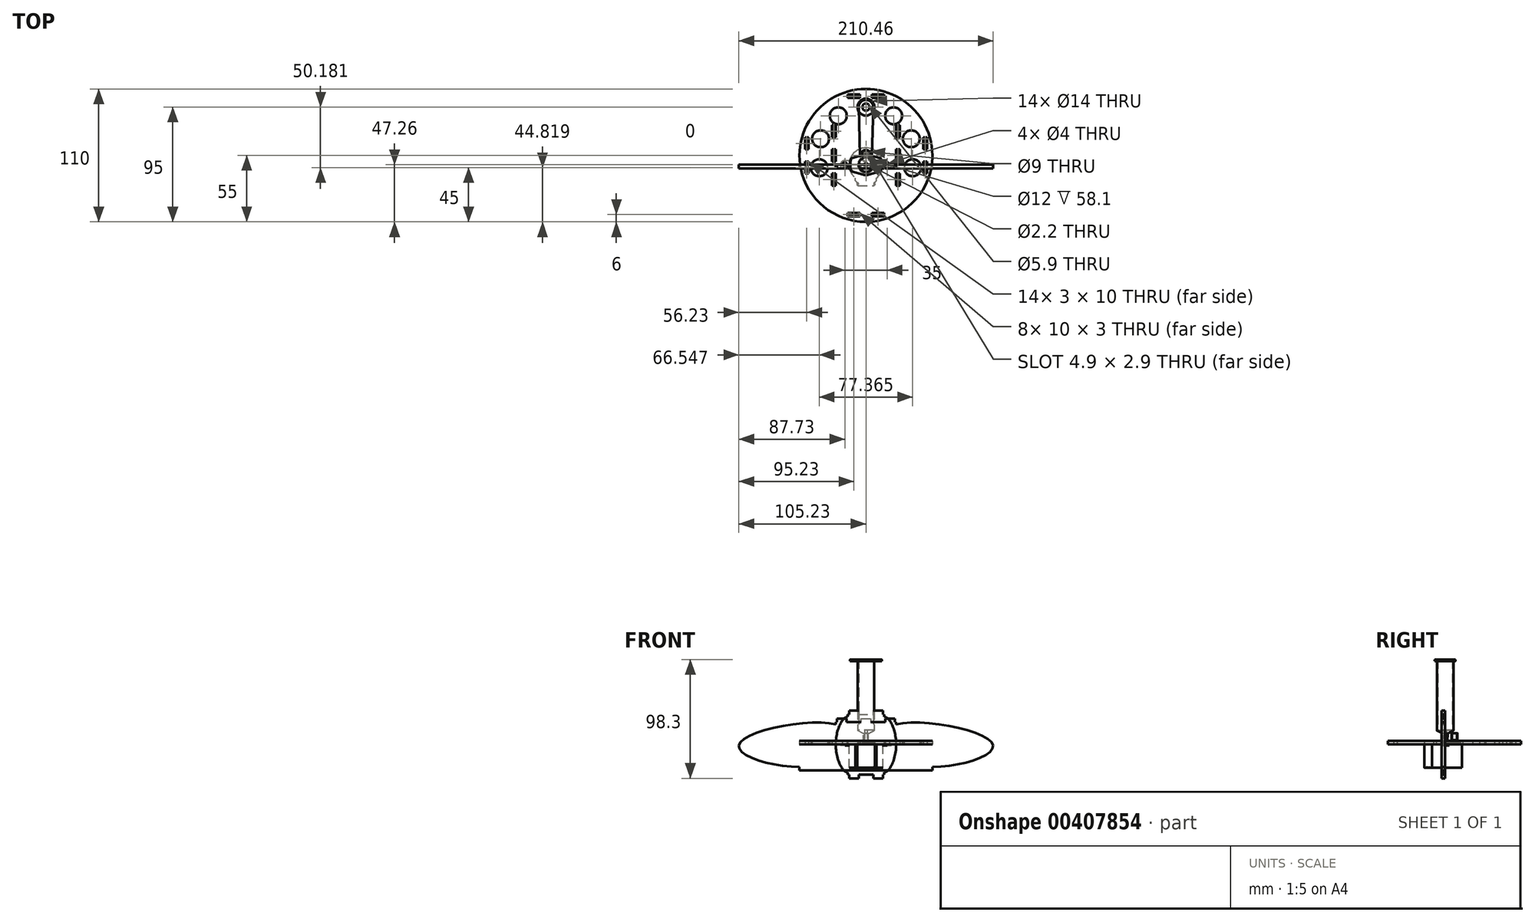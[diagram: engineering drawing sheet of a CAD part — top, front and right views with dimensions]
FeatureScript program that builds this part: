
annotation { "Feature Type Name" : "Feature", "Feature Type Description" : "" }
export const myFeature = defineFeature(function(context is Context, id is Id, definition is map)
    precondition{}
    {
        {
            var Q0;
            Q0=qCreatedBy(makeId("Top.planeOp"),FACE);
            var sketch = newSketch(context, id + "F0", { "sketchPlane" : qUnion([Q0])});
            skCircle(sketch, "E0", {"center": v(0, 0) * mm, "radius": 6.85 * mm});
            skCircle(sketch, "E1", {"center": v(0, 0) * mm, "radius": 1.1 * mm});
            skCircle(sketch, "E2", {"center": v(0, 0) * mm, "radius": 8.5 * mm});
            skLineSegment(sketch, "E3", {"start": v(-1.1, 0) * mm, "end": v(1.1, 0) * mm});
            skLineSegment(sketch, "E4", {"start": v(-11.5, 5.5) * mm, "end": v(-11.4, 5.5) * mm});
            skLineSegment(sketch, "E5", {"start": v(11.5, -5.5) * mm, "end": v(11.4, -5.5) * mm});
            skLineSegment(sketch, "E6", {"start": v(-11.5, 5.5) * mm, "end": v(-2.38, 8.16) * mm});
            skLineSegment(sketch, "E7", {"start": v(-11.5, -5.5) * mm, "end": v(-2.38, -8.16) * mm});
            skLineSegment(sketch, "E8", {"start": v(11.5, -5.5) * mm, "end": v(2.38, -8.16) * mm});
            skLineSegment(sketch, "E9", {"start": v(11.5, 5.5) * mm, "end": v(2.38, 8.16) * mm});
            skFitSpline(sketch, "E10", {"points": [v(-11.5, 5.5) * mm, v(-13.25, 0) * mm, v(-11.5, -5.5) * mm, v(-8.5, 0) * mm, v(-11.5, 5.5) * mm]});
            skFitSpline(sketch, "E11", {"points": [v(11.5, 5.5) * mm, v(13.25, 0) * mm, v(11.5, -5.5) * mm, v(8.5, 0) * mm, v(11.5, 5.5) * mm]});
            skLineSegment(sketch, "E12.trimOffspring", {"start": v(-11.4, -5.5) * mm, "end": v(-11.5, -5.5) * mm});
            skLineSegment(sketch, "E13.trimOffspring", {"start": v(11.4, 5.5) * mm, "end": v(11.5, 5.5) * mm});
            skCircle(sketch, "E14", {"center": v(0, 0) * mm, "radius": 6 * mm});
            skCircle(sketch, "E15", {"center": v(0, 0) * mm, "radius": 2 * mm});
            skSolve(sketch);
        }
        {
            var Q0;
            Q0=qSketchRegion(id+"F0",true);
            extrude(context, id + "F1", {"entities" : qUnion([Q0]), "depth" : 70.3 * mm});
        }
        {
            var Q0;
            Q0=qSketchRegion(id+"F0",true);
            extrude(context, id + "F2", {"entities" : qUnion([Q0]), "operationType" : NewBodyOperationType.REMOVE, "depth" : (70.3 - 1.4) * mm});
        }
        {
            var Q0;
            Q0=makeQuery(id+"F0.imprint","IMPRINT",FACE,{"disambiguationData":[TD([[makeQuery(id+"F0.imprint","IMPRINT",EDGE,{"derivedFrom":sQuery(id+"F0.wireOp",EDGE,"E0")}),1.0]])]});
            extrude(context, id + "F3", {"entities" : qUnion([Q0]), "operationType" : NewBodyOperationType.ADD, "depth" : 70.3 * mm, "hasSecondDirection" : true, "secondDirectionOppositeDirection" : true, "secondDirectionDepth" : -9 * mm});
        }
        {
            var Q0;
            Q0=makeQuery(id+"F0.imprint","IMPRINT",FACE,{"disambiguationData":[TD([[makeQuery(id+"F0.imprint","IMPRINT",EDGE,{"derivedFrom":sQuery(id+"F0.wireOp",EDGE,"E14")}),1.0]])]});
            extrude(context, id + "F4", {"entities" : qUnion([Q0]), "operationType" : NewBodyOperationType.ADD, "depth" : 12 * mm, "hasSecondDirection" : true, "secondDirectionOppositeDirection" : true, "secondDirectionDepth" : -9 * mm});
        }
        {
            var Q0;
            Q0=makeQuery(id+"F0.imprint","IMPRINT",FACE,{"disambiguationData":[TD([[makeQuery(id+"F0.imprint","IMPRINT",EDGE,{"derivedFrom":sQuery(id+"F0.wireOp",EDGE,"E15")}),1.0]])]});
            extrude(context, id + "F5", {"entities" : qUnion([Q0]), "operationType" : NewBodyOperationType.ADD, "depth" : 12 * mm});
        }
        {
            var Q0;
            Q0=makeQuery(id+"F3.opExtrude","CAP_EDGE",EDGE,{"disambiguationData":[OSD([sQuery(id+"F0.wireOp",EDGE,"E0")])],"isStart":true});
            chamfer(context, id + "F6", {"entities" : qUnion([Q0]), "chamferType" : ChamferType.TWO_OFFSETS, "width1" : 2.5 * mm, "oppositeDirection" : false, "width2" : 4.9 * mm, "tangentPropagation" : true});
        }
        {
            var Q0;
            Q0=makeQuery(id+"F5.opExtrude","CAP_EDGE",EDGE,{"disambiguationData":[OSD([sQuery(id+"F0.wireOp",EDGE,"E15")])],"isStart":true});
            chamfer(context, id + "F7", {"entities" : qUnion([Q0]), "chamferType" : ChamferType.TWO_OFFSETS, "width1" : 9 * mm, "oppositeDirection" : false, "width2" : 0.1 * mm, "tangentPropagation" : true});
        }
        {
            var Q0;
            Q0=makeQuery(id+"F5.opExtrude","CAP_EDGE",EDGE,{"disambiguationData":[OSD([sQuery(id+"F0.wireOp",EDGE,"E1")])],"isStart":true});
            var Q1;
            {var subQ0=sQuery(id+"F0.wireOp",EDGE,"E15");Q1=makeQuery(id+"F7.opChamfer","BLEND_EDGE",EDGE,{"blendedFrom":[makeQuery(id+"F5.opExtrude","CAP_EDGE",EDGE,{"disambiguationData":[OSD([subQ0])],"isStart":true}),makeQuery(id+"F5.opExtrude","CAP_FACE",FACE,{"disambiguationData":[OSD([sQuery(id+"F0.wireOp",EDGE,"E1"),subQ0])],"isStart":true})],"blendedInto":[makeQuery(id+"F5.opExtrude","CAP_FACE",FACE,{"disambiguationData":[OSD([sQuery(id+"F0.wireOp",EDGE,"E1"),subQ0])],"isStart":true})]});}
            var Q2;
            {var subQ0=sQuery(id+"F0.wireOp",EDGE,"E0");Q2=makeQuery(id+"F6.opChamfer","BLEND_EDGE",EDGE,{"blendedFrom":[makeQuery(id+"F3.opExtrude","CAP_EDGE",EDGE,{"disambiguationData":[OSD([subQ0])],"isStart":true}),makeQuery(id+"F3.opExtrude","SWEPT_FACE",FACE,{"disambiguationData":[OSD([subQ0])]})],"blendedInto":[makeQuery(id+"F3.opExtrude","SWEPT_FACE",FACE,{"disambiguationData":[OSD([subQ0])]})]});}
            var Q3;
            {var subQ0=sQuery(id+"F0.wireOp",EDGE,"E15");Q3=makeQuery(id+"F7.opChamfer","BLEND_EDGE",EDGE,{"blendedFrom":[makeQuery(id+"F5.opExtrude","CAP_EDGE",EDGE,{"disambiguationData":[OSD([subQ0])],"isStart":true}),makeQuery(id+"F5.opExtrude","SWEPT_FACE",FACE,{"disambiguationData":[OSD([subQ0])]})],"blendedInto":[makeQuery(id+"F5.opExtrude","SWEPT_FACE",FACE,{"disambiguationData":[OSD([subQ0])]})]});}
            var Q4;
            Q4=makeQuery(id+"F3.opExtrude","CAP_EDGE",EDGE,{"disambiguationData":[OSD([sQuery(id+"F0.wireOp",EDGE,"E14")])],"isStart":false});
            var Q5;
            Q5=makeQuery(id+"F1.opExtrude","CAP_EDGE",EDGE,{"disambiguationData":[OSD([sQuery(id+"F0.wireOp",EDGE,"E9")])],"isStart":false});
            var Q6;
            Q6=makeQuery(id+"F1.opExtrude","CAP_EDGE",EDGE,{"disambiguationData":[OSD([sQuery(id+"F0.wireOp",EDGE,"E11")])],"isStart":false});
            var Q7;
            Q7=makeQuery(id+"F1.opExtrude","CAP_EDGE",EDGE,{"disambiguationData":[OSD([sQuery(id+"F0.wireOp",EDGE,"E8")])],"isStart":false});
            var Q8;
            {var subQ0=sQuery(id+"F0.wireOp",EDGE,"E2");Q8=makeQuery(id+"F1.opExtrude","CAP_EDGE",EDGE,{"disambiguationData":[OSD([subQ0]),TDD([makeQuery(id+"F0.imprint","IMPRINT",EDGE,{"disambiguationData":[TD([[makeQuery(id+"F0.imprint","INTERSECT",VERTEX,{"derivedFrom":[subQ0,sQuery(id+"F0.wireOp",EDGE,"E7")]}),-1.0]])],"derivedFrom":subQ0})])],"isStart":false});}
            var Q9;
            Q9=makeQuery(id+"F1.opExtrude","CAP_EDGE",EDGE,{"disambiguationData":[OSD([sQuery(id+"F0.wireOp",EDGE,"E7")])],"isStart":false});
            var Q10;
            Q10=makeQuery(id+"F1.opExtrude","CAP_EDGE",EDGE,{"disambiguationData":[OSD([sQuery(id+"F0.wireOp",EDGE,"E10")])],"isStart":false});
            var Q11;
            Q11=makeQuery(id+"F1.opExtrude","CAP_EDGE",EDGE,{"disambiguationData":[OSD([sQuery(id+"F0.wireOp",EDGE,"E6")])],"isStart":false});
            var Q12;
            {var subQ0=sQuery(id+"F0.wireOp",EDGE,"E2");Q12=makeQuery(id+"F1.opExtrude","CAP_EDGE",EDGE,{"disambiguationData":[OSD([subQ0]),TDD([makeQuery(id+"F0.imprint","IMPRINT",EDGE,{"disambiguationData":[TD([[makeQuery(id+"F0.imprint","INTERSECT",VERTEX,{"derivedFrom":[subQ0,sQuery(id+"F0.wireOp",EDGE,"E6")]}),1.0]])],"derivedFrom":subQ0})])],"isStart":false});}
            var Q13;
            Q13=makeQuery(id+"F2.boolean.opBoolean","COPY",EDGE,{"derivedFrom":makeQuery(id+"F2.opExtrude","CAP_EDGE",EDGE,{"disambiguationData":[OSD([sQuery(id+"F0.wireOp",EDGE,"E7")])],"isStart":false})});
            var Q14;
            {var subQ0=sQuery(id+"F0.wireOp",EDGE,"E2");Q14=makeQuery(id+"F2.boolean.opBoolean","COPY",EDGE,{"derivedFrom":makeQuery(id+"F2.opExtrude","CAP_EDGE",EDGE,{"disambiguationData":[OSD([subQ0]),TDD([makeQuery(id+"F0.imprint","IMPRINT",EDGE,{"disambiguationData":[TD([[makeQuery(id+"F0.imprint","INTERSECT",VERTEX,{"derivedFrom":[subQ0,sQuery(id+"F0.wireOp",EDGE,"E7")]}),-1.0]])],"derivedFrom":subQ0})])],"isStart":false})});}
            var Q15;
            Q15=makeQuery(id+"F2.boolean.opBoolean","COPY",EDGE,{"derivedFrom":makeQuery(id+"F2.opExtrude","CAP_EDGE",EDGE,{"disambiguationData":[OSD([sQuery(id+"F0.wireOp",EDGE,"E8")])],"isStart":false})});
            var Q16;
            Q16=makeQuery(id+"F2.boolean.opBoolean","COPY",EDGE,{"derivedFrom":makeQuery(id+"F2.opExtrude","CAP_EDGE",EDGE,{"disambiguationData":[OSD([sQuery(id+"F0.wireOp",EDGE,"E11")])],"isStart":false})});
            var Q17;
            Q17=makeQuery(id+"F2.boolean.opBoolean","COPY",EDGE,{"derivedFrom":makeQuery(id+"F2.opExtrude","CAP_EDGE",EDGE,{"disambiguationData":[OSD([sQuery(id+"F0.wireOp",EDGE,"E9")])],"isStart":false})});
            var Q18;
            Q18=makeQuery(id+"F2.boolean.opBoolean","COPY",EDGE,{"derivedFrom":makeQuery(id+"F2.opExtrude","CAP_EDGE",EDGE,{"disambiguationData":[OSD([sQuery(id+"F0.wireOp",EDGE,"E10")])],"isStart":false})});
            var Q19;
            Q19=makeQuery(id+"F2.boolean.opBoolean","COPY",EDGE,{"derivedFrom":makeQuery(id+"F2.opExtrude","CAP_EDGE",EDGE,{"disambiguationData":[OSD([sQuery(id+"F0.wireOp",EDGE,"E6")])],"isStart":false})});
            var Q20;
            {var subQ0=sQuery(id+"F0.wireOp",EDGE,"E2");Q20=makeQuery(id+"F2.boolean.opBoolean","COPY",EDGE,{"derivedFrom":makeQuery(id+"F2.opExtrude","CAP_EDGE",EDGE,{"disambiguationData":[OSD([subQ0]),TDD([makeQuery(id+"F0.imprint","IMPRINT",EDGE,{"disambiguationData":[TD([[makeQuery(id+"F0.imprint","INTERSECT",VERTEX,{"derivedFrom":[subQ0,sQuery(id+"F0.wireOp",EDGE,"E6")]}),1.0]])],"derivedFrom":subQ0})])],"isStart":false})});}
            var Q21;
            Q21=makeQuery(id+"F2.boolean.opBoolean","COPY",EDGE,{"derivedFrom":makeQuery(id+"F2.opExtrude","CAP_EDGE",EDGE,{"disambiguationData":[OSD([sQuery(id+"F0.wireOp",EDGE,"E0")])],"isStart":false})});
            fillet(context, id + "F8", {"entities" : qUnion([Q0, Q1, Q2, Q3, Q4, Q5, Q6, Q7, Q8, Q9, Q10, Q11, Q12, Q13, Q14, Q15, Q16, Q17, Q18, Q19, Q20, Q21]), "radius" : 0.2 * mm, "tangentPropagation" : true, "allowEdgeOverflow" : false});
        }
        {
            var Q0;
            Q0=qCreatedBy(makeId("Top.planeOp"),FACE);
            var sketch = newSketch(context, id + "F9", { "sketchPlane" : qUnion([Q0])});
            skCircle(sketch, "E16", {"center": v(0, 0) * mm, "radius": 14 * mm});
            skLineSegment(sketch, "E17", {"start": v(0, 0) * mm, "end": v(0, -13.2) * mm, "construction": true});
            skLineSegment(sketch, "E18", {"start": v(-7.3, -17.2) * mm, "end": v(7.3, -17.2) * mm});
            skLineSegment(sketch, "E19", {"start": v(-7.3, -14.7) * mm, "end": v(7.3, -14.7) * mm, "construction": true});
            skLineSegment(sketch, "E20", {"start": v(7.3, -17.2) * mm, "end": v(7.3, -14.7) * mm});
            skLineSegment(sketch, "E21", {"start": v(-7.3, -17.2) * mm, "end": v(-7.3, -14.7) * mm});
            skLineSegment(sketch, "E22", {"start": v(-8.75, -13.2) * mm, "end": v(-4.66, -13.2) * mm, "construction": true});
            skLineSegment(sketch, "E23", {"start": v(0, -14.7) * mm, "end": v(0, -13.2) * mm});
            skLineSegment(sketch, "E24", {"start": v(7.3, -14.7) * mm, "end": v(8.75, -13.2) * mm});
            skLineSegment(sketch, "E25", {"start": v(8.75, -13.2) * mm, "end": v(8.75, -10.93) * mm});
            skLineSegment(sketch, "E26", {"start": v(-7.3, -14.7) * mm, "end": v(-8.75, -13.2) * mm});
            skLineSegment(sketch, "E27", {"start": v(-8.75, -13.2) * mm, "end": v(-8.75, -10.93) * mm});
            skLineSegment(sketch, "E28", {"start": v(-17.5, 0) * mm, "end": v(17.5, 0) * mm, "construction": true});
            skCircle(sketch, "E29", {"center": v(-17.5, 0) * mm, "radius": 2 * mm});
            skCircle(sketch, "E30", {"center": v(17.5, 0) * mm, "radius": 2 * mm});
            skArc(sketch, "E31", {"start": v(-17.5, 3.5) * mm, "mid": v(-21, 0) * mm, "end": v(-17.5, -3.5) * mm});
            skArc(sketch, "E32", {"start": v(17.5, -3.5) * mm, "mid": v(21, 0) * mm, "end": v(17.5, 3.5) * mm});
            skLineSegment(sketch, "E33", {"start": v(-17.5, 3.5) * mm, "end": v(-13.56, 3.5) * mm});
            skLineSegment(sketch, "E34", {"start": v(-17.5, -3.5) * mm, "end": v(-13.56, -3.5) * mm});
            skLineSegment(sketch, "E35", {"start": v(17.5, -3.5) * mm, "end": v(13.56, -3.5) * mm});
            skLineSegment(sketch, "E36", {"start": v(17.5, 3.5) * mm, "end": v(13.56, 3.5) * mm});
            skCircle(sketch, "E37", {"center": v(0, 7.74) * mm, "radius": 4.5 * mm});
            skCircle(sketch, "E38", {"center": v(0, 7.74) * mm, "radius": 2.45 * mm});
            skLineSegment(sketch, "E39.trimOffspring", {"start": v(4.66, -13.2) * mm, "end": v(8.75, -13.2) * mm, "construction": true});
            skLineSegment(sketch, "E40.trimOffspring", {"start": v(0, -14) * mm, "end": v(0, -17.2) * mm, "construction": true});
            skLineSegment(sketch, "E41", {"start": v(-1.45, 7.74) * mm, "end": v(1.45, 7.74) * mm, "construction": true});
            skLineSegment(sketch, "E42", {"start": v(-1.45, 9.71) * mm, "end": v(-1.45, 5.77) * mm});
            skLineSegment(sketch, "E43", {"start": v(1.45, 9.71) * mm, "end": v(1.45, 5.77) * mm});
            skSolve(sketch);
        }
        {
            var Q0;
            Q0=makeQuery(id+"F9.imprint","IMPRINT",FACE,{"disambiguationData":[TD([[makeQuery(id+"F9.imprint","IMPRINT",EDGE,{"derivedFrom":sQuery(id+"F9.wireOp",EDGE,"E29")}),-1.0]])]});
            var Q1;
            Q1=makeQuery(id+"F9.imprint","IMPRINT",FACE,{"disambiguationData":[TD([[makeQuery(id+"F9.imprint","IMPRINT",EDGE,{"derivedFrom":sQuery(id+"F9.wireOp",EDGE,"E37")}),-1.0]])]});
            var Q2;
            Q2=makeQuery(id+"F9.imprint","IMPRINT",FACE,{"disambiguationData":[TD([[makeQuery(id+"F9.imprint","IMPRINT",EDGE,{"derivedFrom":sQuery(id+"F9.wireOp",EDGE,"E18")}),1.0]])]});
            var Q3;
            Q3=makeQuery(id+"F9.imprint","IMPRINT",FACE,{"disambiguationData":[TD([[makeQuery(id+"F9.imprint","IMPRINT",EDGE,{"derivedFrom":sQuery(id+"F9.wireOp",EDGE,"E30")}),-1.0]])]});
            var Q4;
            Q4=makeQuery(id+"F9.imprint","IMPRINT",FACE,{"disambiguationData":[TD([[makeQuery(id+"F9.imprint","IMPRINT",EDGE,{"derivedFrom":sQuery(id+"F9.wireOp",EDGE,"E37")}),1.0]])]});
            var Q5;
            {var subQ0=sQuery(id+"F9.wireOp",EDGE,"E42");Q5=makeQuery(id+"F9.imprint","IMPRINT",FACE,{"disambiguationData":[TD([[makeQuery(id+"F9.imprint","IMPRINT",EDGE,{"derivedFrom":subQ0}),1.0]])]});}
            var Q6;
            {var subQ0=sQuery(id+"F9.wireOp",EDGE,"E42");Q6=makeQuery(id+"F9.imprint","IMPRINT",FACE,{"disambiguationData":[TD([[makeQuery(id+"F9.imprint","IMPRINT",EDGE,{"derivedFrom":subQ0}),-1.0]])]});}
            var Q7;
            {var subQ0=sQuery(id+"F9.wireOp",EDGE,"E43");Q7=makeQuery(id+"F9.imprint","IMPRINT",FACE,{"disambiguationData":[TD([[makeQuery(id+"F9.imprint","IMPRINT",EDGE,{"derivedFrom":subQ0}),1.0]])]});}
            extrude(context, id + "F10", {"entities" : qUnion([Q0, Q1, Q2, Q3, Q4, Q5, Q6, Q7]), "oppositeDirection" : true, "depth" : 19.3 * mm});
        }
        {
            var Q0;
            Q0=makeQuery(id+"F9.imprint","IMPRINT",FACE,{"disambiguationData":[TD([[makeQuery(id+"F9.imprint","IMPRINT",EDGE,{"derivedFrom":sQuery(id+"F9.wireOp",EDGE,"E29")}),-1.0]])]});
            var Q1;
            Q1=makeQuery(id+"F9.imprint","IMPRINT",FACE,{"disambiguationData":[TD([[makeQuery(id+"F9.imprint","IMPRINT",EDGE,{"derivedFrom":sQuery(id+"F9.wireOp",EDGE,"E30")}),-1.0]])]});
            extrude(context, id + "F11", {"entities" : qUnion([Q0, Q1]), "operationType" : NewBodyOperationType.REMOVE, "endBound" : BoundingType.THROUGH_ALL, "oppositeDirection" : true, "depth" : 25 * mm, "hasSecondDirection" : true, "secondDirectionOppositeDirection" : false, "secondDirectionDepth" : -0.8 * mm});
        }
        {
            var Q0;
            Q0=makeQuery(id+"F9.imprint","IMPRINT",FACE,{"disambiguationData":[TD([[makeQuery(id+"F9.imprint","IMPRINT",EDGE,{"derivedFrom":sQuery(id+"F9.wireOp",EDGE,"E37")}),1.0]])]});
            extrude(context, id + "F12", {"entities" : qUnion([Q0]), "operationType" : NewBodyOperationType.ADD, "depth" : 1.5 * mm});
        }
        {
            var Q0;
            {var subQ0=sQuery(id+"F9.wireOp",EDGE,"E42");Q0=makeQuery(id+"F9.imprint","IMPRINT",FACE,{"disambiguationData":[TD([[makeQuery(id+"F9.imprint","IMPRINT",EDGE,{"derivedFrom":subQ0}),-1.0]])]});}
            var Q1;
            {var subQ0=sQuery(id+"F9.wireOp",EDGE,"E43");Q1=makeQuery(id+"F9.imprint","IMPRINT",FACE,{"disambiguationData":[TD([[makeQuery(id+"F9.imprint","IMPRINT",EDGE,{"derivedFrom":subQ0}),1.0]])]});}
            extrude(context, id + "F13", {"entities" : qUnion([Q0, Q1]), "operationType" : NewBodyOperationType.ADD, "depth" : 3.5 * mm});
        }
        {
            var Q0;
            {var subQ0=sQuery(id+"F9.wireOp",EDGE,"E42");Q0=makeQuery(id+"F9.imprint","IMPRINT",FACE,{"disambiguationData":[TD([[makeQuery(id+"F9.imprint","IMPRINT",EDGE,{"derivedFrom":subQ0}),1.0]])]});}
            extrude(context, id + "F14", {"entities" : qUnion([Q0]), "operationType" : NewBodyOperationType.ADD, "depth" : 9.5 * mm});
        }
        {
            var Q0;
            Q0=makeQuery(id+"F10.opExtrude","CAP_EDGE",EDGE,{"disambiguationData":[OSD([sQuery(id+"F9.wireOp",EDGE,"E18")])],"isStart":false});
            var Q1;
            {var subQ0=sQuery(id+"F9.wireOp",EDGE,"E38");Q1=makeQuery(id+"F14.opExtrude","CAP_EDGE",EDGE,{"disambiguationData":[OSD([subQ0]),TDD([makeQuery(id+"F9.imprint","IMPRINT",EDGE,{"disambiguationData":[TD([[makeQuery(id+"F9.imprint","INTERSECT",VERTEX,{"disambiguationData":[OD(1.0)],"derivedFrom":[subQ0,sQuery(id+"F9.wireOp",EDGE,"E42")]}),-1.0]])],"derivedFrom":subQ0})])],"isStart":false});}
            var Q2;
            {var subQ0=sQuery(id+"F9.wireOp",EDGE,"E42");var subQ1=sQuery(id+"F9.wireOp",EDGE,"E38");Q2=makeQuery(id+"F13.opExtrude","CAP_EDGE",EDGE,{"disambiguationData":[OSD([subQ1]),TDD([makeQuery(id+"F9.imprint","IMPRINT",EDGE,{"disambiguationData":[TD([[makeQuery(id+"F9.imprint","INTERSECT",VERTEX,{"disambiguationData":[OD(0.0)],"derivedFrom":[subQ1,subQ0]}),-1.0]])],"derivedFrom":subQ1})])],"isStart":false});}
            var Q3;
            {var subQ0=sQuery(id+"F9.wireOp",EDGE,"E43");var subQ1=sQuery(id+"F9.wireOp",EDGE,"E38");Q3=makeQuery(id+"F13.opExtrude","CAP_EDGE",EDGE,{"disambiguationData":[OSD([subQ1]),TDD([makeQuery(id+"F9.imprint","IMPRINT",EDGE,{"disambiguationData":[TD([[makeQuery(id+"F9.imprint","INTERSECT",VERTEX,{"disambiguationData":[OD(0.0)],"derivedFrom":[subQ1,subQ0]}),1.0]])],"derivedFrom":subQ1})])],"isStart":false});}
            var Q4;
            {var subQ0=sQuery(id+"F9.wireOp",EDGE,"E38");Q4=makeQuery(id+"F14.opExtrude","CAP_EDGE",EDGE,{"disambiguationData":[OSD([subQ0]),TDD([makeQuery(id+"F9.imprint","IMPRINT",EDGE,{"disambiguationData":[TD([[makeQuery(id+"F9.imprint","INTERSECT",VERTEX,{"disambiguationData":[OD(0.0)],"derivedFrom":[subQ0,sQuery(id+"F9.wireOp",EDGE,"E42")]}),1.0]])],"derivedFrom":subQ0})])],"isStart":false});}
            fillet(context, id + "F15", {"entities" : qUnion([Q0, Q1, Q2, Q3, Q4]), "radius" : 0.3 * mm, "tangentPropagation" : true, "allowEdgeOverflow" : false});
        }
        {
            var Q0;
            Q0=makeQuery(id+"F10.opExtrude","SWEPT_EDGE",EDGE,{"disambiguationData":[OSD([sQuery(id+"F9.wireOp",EDGE,"E18"),sQuery(id+"F9.wireOp",EDGE,"E20")])]});
            var Q1;
            Q1=makeQuery(id+"F10.opExtrude","SWEPT_EDGE",EDGE,{"disambiguationData":[OSD([sQuery(id+"F9.wireOp",EDGE,"E18"),sQuery(id+"F9.wireOp",EDGE,"E21")])]});
            var Q2;
            {var subQ0=sQuery(id+"F9.wireOp",EDGE,"E18");Q2=makeQuery(id+"F15.opFillet","BLEND_EDGE",EDGE,{"blendedFrom":[makeQuery(id+"F10.opExtrude","CAP_EDGE",EDGE,{"disambiguationData":[OSD([subQ0])],"isStart":false}),makeQuery(id+"F10.opExtrude","SWEPT_FACE",FACE,{"disambiguationData":[OSD([subQ0])]})],"blendedInto":[makeQuery(id+"F10.opExtrude","SWEPT_FACE",FACE,{"disambiguationData":[OSD([subQ0])]})]});}
            fillet(context, id + "F16", {"entities" : qUnion([Q0, Q1, Q2]), "radius" : 1 * mm, "tangentPropagation" : true, "allowEdgeOverflow" : false});
        }
        {
            var Q0;
            Q0=makeQuery(id+"F10.opExtrude","SWEPT_EDGE",EDGE,{"disambiguationData":[OSD([sQuery(id+"F9.wireOp",EDGE,"E26"),sQuery(id+"F9.wireOp",EDGE,"E27")])]});
            var Q1;
            Q1=makeQuery(id+"F10.opExtrude","SWEPT_EDGE",EDGE,{"disambiguationData":[OSD([sQuery(id+"F9.wireOp",EDGE,"E21"),sQuery(id+"F9.wireOp",EDGE,"E26")])]});
            var Q2;
            Q2=makeQuery(id+"F10.opExtrude","SWEPT_EDGE",EDGE,{"disambiguationData":[OSD([sQuery(id+"F9.wireOp",EDGE,"E24"),sQuery(id+"F9.wireOp",EDGE,"E25")])]});
            var Q3;
            Q3=makeQuery(id+"F10.opExtrude","SWEPT_EDGE",EDGE,{"disambiguationData":[OSD([sQuery(id+"F9.wireOp",EDGE,"E20"),sQuery(id+"F9.wireOp",EDGE,"E24")])]});
            var Q4;
            Q4=makeQuery(id+"F16.opFillet","BLEND_EDGE",EDGE,{"blendedFrom":[makeQuery(id+"F10.opExtrude","CAP_EDGE",EDGE,{"disambiguationData":[OSD([sQuery(id+"F9.wireOp",EDGE,"E20")])],"isStart":false}),makeQuery(id+"F10.opExtrude","SWEPT_FACE",FACE,{"disambiguationData":[OSD([sQuery(id+"F9.wireOp",EDGE,"E24")])]})],"blendedInto":[makeQuery(id+"F10.opExtrude","SWEPT_FACE",FACE,{"disambiguationData":[OSD([sQuery(id+"F9.wireOp",EDGE,"E24")])]})]});
            var Q5;
            Q5=makeQuery(id+"F16.opFillet","BLEND_EDGE",EDGE,{"blendedFrom":[makeQuery(id+"F10.opExtrude","CAP_EDGE",EDGE,{"disambiguationData":[OSD([sQuery(id+"F9.wireOp",EDGE,"E21")])],"isStart":false}),makeQuery(id+"F10.opExtrude","SWEPT_FACE",FACE,{"disambiguationData":[OSD([sQuery(id+"F9.wireOp",EDGE,"E26")])]})],"blendedInto":[makeQuery(id+"F10.opExtrude","SWEPT_FACE",FACE,{"disambiguationData":[OSD([sQuery(id+"F9.wireOp",EDGE,"E26")])]})]});
            var Q6;
            Q6=makeQuery(id+"F10.opExtrude","CAP_EDGE",EDGE,{"disambiguationData":[OSD([sQuery(id+"F9.wireOp",EDGE,"E24")])],"isStart":false});
            var Q7;
            Q7=makeQuery(id+"F10.opExtrude","CAP_EDGE",EDGE,{"disambiguationData":[OSD([sQuery(id+"F9.wireOp",EDGE,"E26")])],"isStart":false});
            fillet(context, id + "F17", {"entities" : qUnion([Q0, Q1, Q2, Q3, Q4, Q5, Q6, Q7]), "radius" : 0.3 * mm, "tangentPropagation" : true, "allowEdgeOverflow" : false});
        }
        {
            var Q0;
            Q0=qCreatedBy(makeId("Top.planeOp"),FACE);
            var sketch = newSketch(context, id + "F18", { "sketchPlane" : qUnion([Q0])});
            skCircle(sketch, "E44.0", {"center": v(-17.5, 0) * mm, "radius": 2 * mm});
            skCircle(sketch, "E45.0", {"center": v(0, 7.74) * mm, "radius": 4.5 * mm});
            skCircle(sketch, "E46.0", {"center": v(17.5, 0) * mm, "radius": 2 * mm});
            skCircle(sketch, "E47", {"center": v(0, 7.74) * mm, "radius": 55 * mm});
            skCircle(sketch, "E48", {"center": v(0, 7.74) * mm, "radius": 40 * mm, "construction": true});
            skCircle(sketch, "E49", {"center": v(0, 47.74) * mm, "radius": 7 * mm});
            skCircle(sketch, "E50", {"center": v(-22.9, 40.54) * mm, "radius": 7 * mm});
            skCircle(sketch, "E51", {"center": v(-37.55, 21.53) * mm, "radius": 7 * mm});
            skCircle(sketch, "E52", {"center": v(22.9, 40.54) * mm, "radius": 7 * mm});
            skCircle(sketch, "E53", {"center": v(37.55, 21.53) * mm, "radius": 7 * mm});
            skCircle(sketch, "E54", {"center": v(38.68, -2.44) * mm, "radius": 7 * mm});
            skCircle(sketch, "E55", {"center": v(-38.68, -2.44) * mm, "radius": 7 * mm});
            skLineSegment(sketch, "E56", {"start": v(-49, 7.74) * mm, "end": v(49, 7.74) * mm, "construction": true});
            skLineSegment(sketch, "E57.bottom", {"start": v(-50.5, 2.74) * mm, "end": v(-47.5, 2.74) * mm});
            skLineSegment(sketch, "E57.top", {"start": v(-50.5, -7.26) * mm, "end": v(-47.5, -7.26) * mm});
            skLineSegment(sketch, "E57.left", {"start": v(-50.5, 2.74) * mm, "end": v(-50.5, -7.26) * mm});
            skLineSegment(sketch, "E57.right", {"start": v(-47.5, 2.74) * mm, "end": v(-47.5, -7.26) * mm});
            skLineSegment(sketch, "E58.bottom", {"start": v(47.5, 2.74) * mm, "end": v(50.5, 2.74) * mm});
            skLineSegment(sketch, "E58.top", {"start": v(47.5, -7.26) * mm, "end": v(50.5, -7.26) * mm});
            skLineSegment(sketch, "E58.left", {"start": v(47.5, 2.74) * mm, "end": v(47.5, -7.26) * mm});
            skLineSegment(sketch, "E58.right", {"start": v(50.5, 2.74) * mm, "end": v(50.5, -7.26) * mm});
            skLineSegment(sketch, "E59.bottom", {"start": v(-50.5, 22.74) * mm, "end": v(-47.5, 22.74) * mm});
            skLineSegment(sketch, "E59.top", {"start": v(-50.5, 12.74) * mm, "end": v(-47.5, 12.74) * mm});
            skLineSegment(sketch, "E59.left", {"start": v(-50.5, 22.74) * mm, "end": v(-50.5, 12.74) * mm});
            skLineSegment(sketch, "E59.right", {"start": v(-47.5, 22.74) * mm, "end": v(-47.5, 12.74) * mm});
            skLineSegment(sketch, "E60.bottom", {"start": v(47.5, 22.74) * mm, "end": v(50.5, 22.74) * mm});
            skLineSegment(sketch, "E60.top", {"start": v(47.5, 12.74) * mm, "end": v(50.5, 12.74) * mm});
            skLineSegment(sketch, "E60.left", {"start": v(47.5, 22.74) * mm, "end": v(47.5, 12.74) * mm});
            skLineSegment(sketch, "E60.right", {"start": v(50.5, 22.74) * mm, "end": v(50.5, 12.74) * mm});
            skLineSegment(sketch, "E61", {"start": v(0, 56.74) * mm, "end": v(0, -41.26) * mm, "construction": true});
            skLineSegment(sketch, "E62", {"start": v(-49, 12.74) * mm, "end": v(-49, 2.74) * mm, "construction": true});
            skLineSegment(sketch, "E63", {"start": v(49, 12.74) * mm, "end": v(49, 2.74) * mm, "construction": true});
            skLineSegment(sketch, "E64", {"start": v(-5, 56.74) * mm, "end": v(5, 56.74) * mm, "construction": true});
            skLineSegment(sketch, "E65", {"start": v(-5, -41.26) * mm, "end": v(5, -41.26) * mm, "construction": true});
            skLineSegment(sketch, "E66.bottom", {"start": v(-15, 58.24) * mm, "end": v(-5, 58.24) * mm});
            skLineSegment(sketch, "E66.top", {"start": v(-15, 55.24) * mm, "end": v(-5, 55.24) * mm});
            skLineSegment(sketch, "E66.left", {"start": v(-15, 58.24) * mm, "end": v(-15, 55.24) * mm});
            skLineSegment(sketch, "E66.right", {"start": v(-5, 58.24) * mm, "end": v(-5, 55.24) * mm});
            skLineSegment(sketch, "E67.bottom", {"start": v(5, 58.24) * mm, "end": v(15, 58.24) * mm});
            skLineSegment(sketch, "E67.top", {"start": v(5, 55.24) * mm, "end": v(15, 55.24) * mm});
            skLineSegment(sketch, "E67.left", {"start": v(5, 58.24) * mm, "end": v(5, 55.24) * mm});
            skLineSegment(sketch, "E67.right", {"start": v(15, 58.24) * mm, "end": v(15, 55.24) * mm});
            skLineSegment(sketch, "E68.bottom", {"start": v(5, -39.76) * mm, "end": v(15, -39.76) * mm});
            skLineSegment(sketch, "E68.top", {"start": v(5, -42.76) * mm, "end": v(15, -42.76) * mm});
            skLineSegment(sketch, "E68.left", {"start": v(5, -39.76) * mm, "end": v(5, -42.76) * mm});
            skLineSegment(sketch, "E68.right", {"start": v(15, -39.76) * mm, "end": v(15, -42.76) * mm});
            skLineSegment(sketch, "E69.bottom", {"start": v(-15, -39.76) * mm, "end": v(-5, -39.76) * mm});
            skLineSegment(sketch, "E69.top", {"start": v(-15, -42.76) * mm, "end": v(-5, -42.76) * mm});
            skLineSegment(sketch, "E69.left", {"start": v(-15, -39.76) * mm, "end": v(-15, -42.76) * mm});
            skLineSegment(sketch, "E69.right", {"start": v(-5, -39.76) * mm, "end": v(-5, -42.76) * mm});
            skSolve(sketch);
        }
        {
            var Q0;
            Q0=qSketchRegion(id+"F18",true);
            extrude(context, id + "F19", {"entities" : qUnion([Q0]), "depth" : 3 * mm});
        }
        {
            var Q0;
            Q0=qCreatedBy(makeId("Top.planeOp"),FACE);
            var sketch = newSketch(context, id + "F20", { "sketchPlane" : qUnion([Q0])});
            skCircle(sketch, "E70.0.0", {"center": v(38.68, -2.44) * mm, "radius": 7 * mm});
            skCircle(sketch, "E71.0.0", {"center": v(37.55, 21.53) * mm, "radius": 7 * mm});
            skCircle(sketch, "E72.0.0", {"center": v(22.9, 40.54) * mm, "radius": 7 * mm});
            skLineSegment(sketch, "E73.0.0", {"start": v(5, 58.24) * mm, "end": v(5, 55.24) * mm});
            skLineSegment(sketch, "E73.0.1", {"start": v(5, 55.24) * mm, "end": v(15, 55.24) * mm});
            skLineSegment(sketch, "E73.0.2", {"start": v(15, 55.24) * mm, "end": v(15, 58.24) * mm});
            skLineSegment(sketch, "E73.0.3", {"start": v(15, 58.24) * mm, "end": v(5, 58.24) * mm});
            skLineSegment(sketch, "E74.0.0", {"start": v(-15, 58.24) * mm, "end": v(-15, 55.24) * mm});
            skLineSegment(sketch, "E74.0.1", {"start": v(-15, 55.24) * mm, "end": v(-5, 55.24) * mm});
            skLineSegment(sketch, "E74.0.2", {"start": v(-5, 55.24) * mm, "end": v(-5, 58.24) * mm});
            skLineSegment(sketch, "E74.0.3", {"start": v(-5, 58.24) * mm, "end": v(-15, 58.24) * mm});
            skCircle(sketch, "E75.0", {"center": v(0, 47.74) * mm, "radius": 7 * mm});
            skCircle(sketch, "E76.0", {"center": v(-22.9, 40.54) * mm, "radius": 7 * mm});
            skCircle(sketch, "E77.0", {"center": v(-37.55, 21.53) * mm, "radius": 7 * mm});
            skCircle(sketch, "E78.0", {"center": v(-38.68, -2.44) * mm, "radius": 7 * mm});
            skLineSegment(sketch, "E79.0.0", {"start": v(-50.5, 2.74) * mm, "end": v(-50.5, -7.26) * mm});
            skLineSegment(sketch, "E79.0.1", {"start": v(-50.5, -7.26) * mm, "end": v(-47.5, -7.26) * mm});
            skLineSegment(sketch, "E79.0.2", {"start": v(-47.5, -7.26) * mm, "end": v(-47.5, 2.74) * mm});
            skLineSegment(sketch, "E79.0.3", {"start": v(-47.5, 2.74) * mm, "end": v(-50.5, 2.74) * mm});
            skLineSegment(sketch, "E80.0.0", {"start": v(-50.5, 22.74) * mm, "end": v(-50.5, 12.74) * mm});
            skLineSegment(sketch, "E80.0.1", {"start": v(-50.5, 12.74) * mm, "end": v(-47.5, 12.74) * mm});
            skLineSegment(sketch, "E80.0.2", {"start": v(-47.5, 12.74) * mm, "end": v(-47.5, 22.74) * mm});
            skLineSegment(sketch, "E80.0.3", {"start": v(-47.5, 22.74) * mm, "end": v(-50.5, 22.74) * mm});
            skLineSegment(sketch, "E81.0.0", {"start": v(47.5, 22.74) * mm, "end": v(47.5, 12.74) * mm});
            skLineSegment(sketch, "E81.0.1", {"start": v(47.5, 12.74) * mm, "end": v(50.5, 12.74) * mm});
            skLineSegment(sketch, "E81.0.2", {"start": v(50.5, 12.74) * mm, "end": v(50.5, 22.74) * mm});
            skLineSegment(sketch, "E81.0.3", {"start": v(50.5, 22.74) * mm, "end": v(47.5, 22.74) * mm});
            skLineSegment(sketch, "E82.0.0", {"start": v(47.5, 2.74) * mm, "end": v(47.5, -7.26) * mm});
            skLineSegment(sketch, "E82.0.1", {"start": v(47.5, -7.26) * mm, "end": v(50.5, -7.26) * mm});
            skLineSegment(sketch, "E82.0.2", {"start": v(50.5, -7.26) * mm, "end": v(50.5, 2.74) * mm});
            skLineSegment(sketch, "E82.0.3", {"start": v(50.5, 2.74) * mm, "end": v(47.5, 2.74) * mm});
            skLineSegment(sketch, "E83.0.0", {"start": v(5, -39.76) * mm, "end": v(5, -42.76) * mm});
            skLineSegment(sketch, "E83.0.1", {"start": v(5, -42.76) * mm, "end": v(15, -42.76) * mm});
            skLineSegment(sketch, "E83.0.2", {"start": v(15, -42.76) * mm, "end": v(15, -39.76) * mm});
            skLineSegment(sketch, "E83.0.3", {"start": v(15, -39.76) * mm, "end": v(5, -39.76) * mm});
            skLineSegment(sketch, "E84.0.0", {"start": v(-15, -39.76) * mm, "end": v(-15, -42.76) * mm});
            skLineSegment(sketch, "E84.0.1", {"start": v(-15, -42.76) * mm, "end": v(-5, -42.76) * mm});
            skLineSegment(sketch, "E84.0.2", {"start": v(-5, -42.76) * mm, "end": v(-5, -39.76) * mm});
            skLineSegment(sketch, "E84.0.3", {"start": v(-5, -39.76) * mm, "end": v(-15, -39.76) * mm});
            skCircle(sketch, "E85.0", {"center": v(0, 7.74) * mm, "radius": 55 * mm});
            skLineSegment(sketch, "E86", {"start": v(-25, 7.74) * mm, "end": v(25, 7.74) * mm, "construction": true});
            skLineSegment(sketch, "E87.bottom", {"start": v(-28, 12.74) * mm, "end": v(-25, 12.74) * mm});
            skLineSegment(sketch, "E87.top", {"start": v(-28, 2.74) * mm, "end": v(-25, 2.74) * mm});
            skLineSegment(sketch, "E87.left", {"start": v(-28, 12.74) * mm, "end": v(-28, 2.74) * mm});
            skLineSegment(sketch, "E87.right", {"start": v(-25, 12.74) * mm, "end": v(-25, 2.74) * mm});
            skLineSegment(sketch, "E88.bottom", {"start": v(-28, -7.26) * mm, "end": v(-25, -7.26) * mm});
            skLineSegment(sketch, "E88.top", {"start": v(-28, -17.26) * mm, "end": v(-25, -17.26) * mm});
            skLineSegment(sketch, "E88.left", {"start": v(-28, -7.26) * mm, "end": v(-28, -17.26) * mm});
            skLineSegment(sketch, "E88.right", {"start": v(-25, -7.26) * mm, "end": v(-25, -17.26) * mm});
            skLineSegment(sketch, "E89.bottom", {"start": v(-28, 32.74) * mm, "end": v(-25, 32.74) * mm});
            skLineSegment(sketch, "E89.top", {"start": v(-28, 22.74) * mm, "end": v(-25, 22.74) * mm});
            skLineSegment(sketch, "E89.left", {"start": v(-28, 32.74) * mm, "end": v(-28, 22.74) * mm});
            skLineSegment(sketch, "E89.right", {"start": v(-25, 32.74) * mm, "end": v(-25, 22.74) * mm});
            skLineSegment(sketch, "E90.bottom", {"start": v(25, 12.74) * mm, "end": v(28, 12.74) * mm});
            skLineSegment(sketch, "E90.top", {"start": v(25, 2.74) * mm, "end": v(28, 2.74) * mm});
            skLineSegment(sketch, "E90.left", {"start": v(25, 12.74) * mm, "end": v(25, 2.74) * mm});
            skLineSegment(sketch, "E90.right", {"start": v(28, 12.74) * mm, "end": v(28, 2.74) * mm});
            skLineSegment(sketch, "E91.bottom", {"start": v(25, 32.74) * mm, "end": v(28, 32.74) * mm});
            skLineSegment(sketch, "E91.top", {"start": v(25, 22.74) * mm, "end": v(28, 22.74) * mm});
            skLineSegment(sketch, "E91.left", {"start": v(25, 32.74) * mm, "end": v(25, 22.74) * mm});
            skLineSegment(sketch, "E91.right", {"start": v(28, 32.74) * mm, "end": v(28, 22.74) * mm});
            skLineSegment(sketch, "E92.bottom", {"start": v(25, -7.26) * mm, "end": v(28, -7.26) * mm});
            skLineSegment(sketch, "E92.top", {"start": v(25, -17.26) * mm, "end": v(28, -17.26) * mm});
            skLineSegment(sketch, "E92.left", {"start": v(25, -7.26) * mm, "end": v(25, -17.26) * mm});
            skLineSegment(sketch, "E92.right", {"start": v(28, -7.26) * mm, "end": v(28, -17.26) * mm});
            skLineSegment(sketch, "E93", {"start": v(-26.5, 2.74) * mm, "end": v(-26.5, -7.26) * mm, "construction": true});
            skLineSegment(sketch, "E94", {"start": v(-26.5, 22.74) * mm, "end": v(-26.5, 12.74) * mm, "construction": true});
            skLineSegment(sketch, "E95", {"start": v(26.5, 22.74) * mm, "end": v(26.5, 12.74) * mm, "construction": true});
            skLineSegment(sketch, "E96", {"start": v(26.5, 2.74) * mm, "end": v(26.5, -7.26) * mm, "construction": true});
            skSolve(sketch);
        }
        {
            var Q0;
            Q0=qSketchRegion(id+"F20",true);
            extrude(context, id + "F21", {"entities" : qUnion([Q0]), "depth" : 3 * mm});
        }
        {
            var Q0;
            Q0=qCreatedBy(makeId("Front.planeOp"),FACE);
            var sketch = newSketch(context, id + "F22", { "sketchPlane" : qUnion([Q0])});
            skLineSegment(sketch, "E97", {"start": v(-15, 25) * mm, "end": v(-14, 25) * mm});
            skLineSegment(sketch, "E98", {"start": v(-14, 25) * mm, "end": v(-14, 28) * mm});
            skLineSegment(sketch, "E99", {"start": v(-14, 28) * mm, "end": v(-6, 28) * mm});
            skLineSegment(sketch, "E100", {"start": v(-6, 28) * mm, "end": v(-6, 25) * mm});
            skLineSegment(sketch, "E101", {"start": v(-15, 25) * mm, "end": v(-15, 23) * mm});
            skLineSegment(sketch, "E102", {"start": v(-6, 25) * mm, "end": v(6, 25) * mm});
            skLineSegment(sketch, "E103", {"start": v(6, 25) * mm, "end": v(6, 28) * mm});
            skLineSegment(sketch, "E104", {"start": v(6, 28) * mm, "end": v(14, 28) * mm});
            skLineSegment(sketch, "E105", {"start": v(14, 28) * mm, "end": v(14, 25) * mm});
            skLineSegment(sketch, "E106", {"start": v(14, 25) * mm, "end": v(15, 25) * mm});
            skLineSegment(sketch, "E107", {"start": v(15, 25) * mm, "end": v(15, 23) * mm});
            skLineSegment(sketch, "E108", {"start": v(0, 25) * mm, "end": v(0, -25) * mm, "construction": true});
            skLineSegment(sketch, "E109", {"start": v(-6, -25) * mm, "end": v(6, -25) * mm});
            skLineSegment(sketch, "E110", {"start": v(6, -25) * mm, "end": v(6, -28) * mm});
            skLineSegment(sketch, "E111", {"start": v(6, -28) * mm, "end": v(14, -28) * mm});
            skLineSegment(sketch, "E112", {"start": v(14, -28) * mm, "end": v(14, -25) * mm});
            skLineSegment(sketch, "E113", {"start": v(14, -25) * mm, "end": v(15, -25) * mm});
            skLineSegment(sketch, "E114", {"start": v(15, -25) * mm, "end": v(15, -23) * mm});
            skLineSegment(sketch, "E115", {"start": v(-6, -25) * mm, "end": v(-6, -28) * mm});
            skLineSegment(sketch, "E116", {"start": v(-6, -28) * mm, "end": v(-14, -28) * mm});
            skLineSegment(sketch, "E117", {"start": v(-14, -28) * mm, "end": v(-14, -25) * mm});
            skLineSegment(sketch, "E118", {"start": v(-14, -25) * mm, "end": v(-15, -25) * mm});
            skLineSegment(sketch, "E119", {"start": v(-15, -25) * mm, "end": v(-15, -23) * mm});
            skLineSegment(sketch, "E120", {"start": v(-5, 0) * mm, "end": v(5, 0) * mm, "construction": true});
            skLineSegment(sketch, "E121", {"start": v(-5, 0) * mm, "end": v(-25, 0) * mm, "construction": true});
            skLineSegment(sketch, "E122", {"start": v(5, 0) * mm, "end": v(25, 0) * mm, "construction": true});
            skFitSpline(sketch, "E123", {"points": [v(-15, 23) * mm, v(-5, 0) * mm, v(-15, -23) * mm, v(-25, 0) * mm, v(-15, 23) * mm]});
            skFitSpline(sketch, "E124", {"points": [v(15, 23) * mm, v(5, 0) * mm, v(15, -23) * mm, v(25, 0) * mm, v(15, 23) * mm]});
            skSolve(sketch);
        }
        {
            var Q0;
            Q0=qSketchRegion(id+"F22",true);
            extrude(context, id + "F23", {"entities" : qUnion([Q0]), "depth" : 3 * mm});
        }
        {
            var Q0;
            Q0=qCreatedBy(makeId("Front.planeOp"),FACE);
            var sketch = newSketch(context, id + "F24", { "sketchPlane" : qUnion([Q0])});
            skLineSegment(sketch, "E125", {"start": v(0, 21.5) * mm, "end": v(0, -21.5) * mm, "construction": true});
            skLineSegment(sketch, "E126", {"start": v(-55, -21.5) * mm, "end": v(55, -21.5) * mm});
            skLineSegment(sketch, "E127", {"start": v(-24, 21.5) * mm, "end": v(-16, 21.5) * mm});
            skLineSegment(sketch, "E128", {"start": v(-16, 21.5) * mm, "end": v(-16, 18.5) * mm});
            skLineSegment(sketch, "E129", {"start": v(-16, 18.5) * mm, "end": v(-4, 18.5) * mm});
            skLineSegment(sketch, "E130", {"start": v(-4, 18.5) * mm, "end": v(-4, 21.5) * mm});
            skLineSegment(sketch, "E131", {"start": v(-4, 21.5) * mm, "end": v(4, 21.5) * mm});
            skLineSegment(sketch, "E132", {"start": v(4, 21.5) * mm, "end": v(4, 18.5) * mm});
            skLineSegment(sketch, "E133", {"start": v(16, 18.5) * mm, "end": v(16, 21.5) * mm});
            skLineSegment(sketch, "E134", {"start": v(16, 21.5) * mm, "end": v(24, 21.5) * mm});
            skLineSegment(sketch, "E135", {"start": v(24, 21.5) * mm, "end": v(24, 18.5) * mm});
            skLineSegment(sketch, "E136", {"start": v(24, 18.5) * mm, "end": v(25, 18.5) * mm});
            skLineSegment(sketch, "E137", {"start": v(16, 18.5) * mm, "end": v(4, 18.5) * mm});
            skLineSegment(sketch, "E138", {"start": v(-24, 21.5) * mm, "end": v(-24, 18.5) * mm});
            skLineSegment(sketch, "E139", {"start": v(-24, 18.5) * mm, "end": v(-25, 18.5) * mm});
            skLineSegment(sketch, "E140", {"start": v(-25, 18.5) * mm, "end": v(-25, 16.5) * mm});
            skLineSegment(sketch, "E141", {"start": v(25, 18.5) * mm, "end": v(25, 16.5) * mm});
            skLineSegment(sketch, "E142", {"start": v(-55, -21.5) * mm, "end": v(-55, -18.5) * mm});
            skLineSegment(sketch, "E143", {"start": v(55, -21.5) * mm, "end": v(55, -18.5) * mm});
            skLineSegment(sketch, "E144", {"start": v(-15, 0) * mm, "end": v(15, 0) * mm, "construction": true});
            skLineSegment(sketch, "E145", {"start": v(-15, 0) * mm, "end": v(-105, 0) * mm, "construction": true});
            skLineSegment(sketch, "E146", {"start": v(15, 0) * mm, "end": v(105, 0) * mm, "construction": true});
            skFitSpline(sketch, "E147", {"points": [v(-25, 16.5) * mm, v(-15, 0) * mm, v(-55, -18.5) * mm, v(-105, 0) * mm, v(-25, 16.5) * mm]});
            skFitSpline(sketch, "E148", {"points": [v(25, 16.5) * mm, v(15, 0) * mm, v(55, -18.5) * mm, v(105, 0) * mm, v(25, 16.5) * mm]});
            skSolve(sketch);
        }
        {
            var Q0;
            Q0=qSketchRegion(id+"F24",true);
            extrude(context, id + "F25", {"entities" : qUnion([Q0]), "depth" : 3 * mm});
        }
        {
            var Q0;
            Q0=qCreatedBy(makeId("Top.planeOp"),FACE);
            var sketch = newSketch(context, id + "F26", { "sketchPlane" : qUnion([Q0])});
            skArc(sketch, "E149.0", {"start": v(1.45, 9.71) * mm, "mid": v(0, 10.2) * mm, "end": v(-1.45, 9.71) * mm});
            skLineSegment(sketch, "E150.0", {"start": v(-1.45, 9.71) * mm, "end": v(-1.45, 5.77) * mm});
            skLineSegment(sketch, "E151.0", {"start": v(1.45, 9.71) * mm, "end": v(1.45, 5.77) * mm});
            skArc(sketch, "E152", {"start": v(6, 47.6) * mm, "mid": v(0, 53.74) * mm, "end": v(-6, 47.6) * mm});
            skArc(sketch, "E153", {"start": v(-5, 7.62) * mm, "mid": v(0, 2.74) * mm, "end": v(5, 7.61) * mm});
            skCircle(sketch, "E154", {"center": v(0, 47.74) * mm, "radius": 2.95 * mm});
            skLineSegment(sketch, "E155", {"start": v(-6, 47.6) * mm, "end": v(-5, 7.61) * mm});
            skLineSegment(sketch, "E156", {"start": v(5, 7.61) * mm, "end": v(6, 47.6) * mm});
            skArc(sketch, "E157.trimOffspring", {"start": v(-1.45, 5.77) * mm, "mid": v(0, 5.29) * mm, "end": v(1.45, 5.77) * mm});
            skSolve(sketch);
        }
        {
            var Q0;
            Q0=qSketchRegion(id+"F26",true);
            extrude(context, id + "F27", {"entities" : qUnion([Q0]), "depth" : 3 * mm});
        }
    });
